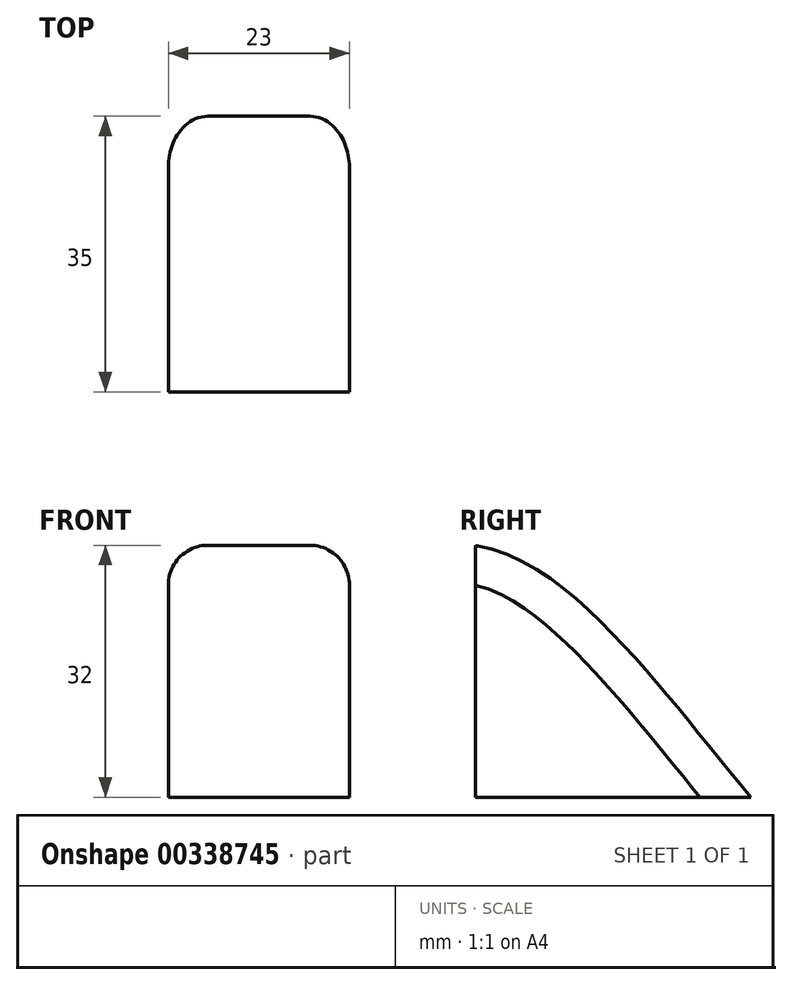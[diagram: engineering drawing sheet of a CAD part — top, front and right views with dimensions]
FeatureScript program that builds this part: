
annotation { "Feature Type Name" : "Feature", "Feature Type Description" : "" }
export const myFeature = defineFeature(function(context is Context, id is Id, definition is map)
    precondition{}
    {
        {
            var Q0;
            Q0=qCreatedBy(makeId("Right.planeOp"),FACE);
            var sketch = newSketch(context, id + "F0", { "sketchPlane" : qUnion([Q0])});
            skLineSegment(sketch, "E0", {"start": v(0, 0) * mm, "end": v(0, 32) * mm});
            skFitSpline(sketch, "E1", {"points": [v(0, 32) * mm, v(17.15, 21.05) * mm, v(35, 0) * mm], "startDerivative": vector(39.73, -5.69) * mm, "endDerivative": vector(37.1, -44.65) * mm});
            skLineSegment(sketch, "E2", {"start": v(35, 0) * mm, "end": v(0, 0) * mm});
            skSolve(sketch);
        }
        {
            var Q0;
            Q0 = qSketchRegion(id + "F0", true);
            extrude(context, id + "F1", {"entities" : qUnion([Q0]), "depth" : 23 * mm});
        }
        {
            var Q0;
            Q0=makeQuery(id+"F1.opExtrude","CAP_EDGE",EDGE,{"disambiguationData":[OSD([sQuery(id+"F0.wireOp",EDGE,"E1")])],"isStart":false});
            var Q1;
            Q1=makeQuery(id+"F1.opExtrude","CAP_EDGE",EDGE,{"disambiguationData":[OSD([sQuery(id+"F0.wireOp",EDGE,"E1")])],"isStart":true});
            fillet(context, id + "F2", {"entities" : qUnion([Q0, Q1]), "radius" : 5 * mm, "tangentPropagation" : true, "allowEdgeOverflow" : false});
        }
    });
